# Revit family: Deca_Acabamento para Registro de Gaveta Duna Quadratta_4900.C94.GD
name_source: partatom
category: Plumbing Fixtures
revit_build: Autodesk Revit Architecture 2012 (Build: 20120126_0600(x64)
units: mm (PartAtom-declared; Revit-internal decimal feet)

## types (4) — shared parameters
Aprovado por = Contino/quattroD
Assembly Code = D2020
Atendimento ao Cliente = 0800-0117073
Consumo = Varia com a pressão
Criado por = Contino/quattroD
Description = Acabamento para registro de gaveta
Flow Pressure = 0.00 psi
Linha = Duna Quadratta
Louça/Metais = Metal
Manufacturer = Deca
Material = Deca_Latão Cromado e Plástico de Engenharia
Norma = ABNT NBR 10283: 2003
Peso Liquido (Kg) = 2.96
Pressão = 2 A 40 mca
Produto = Acabamento para registro de gaveta Duna Quadratta
Segmento = Luxo
URL = www.deca.com.br/produtos
Variações de COR = Cromado 1 1/4 e 1 1/2  (4900.C94.GD); Gold 1 1/4 e 1 1/2  (4900.D94.GD.GLD)
zero-valued in all types: CWFU, Default Elevation

## per-type parameters (varying)
| type | Acabamento | Base de Registro de Gaveta_Family | Código | Diâmetro Ponto de Agua | Model | Raio Ponto de Agua |
| 4900.C94.GD_Cromado CR10_1 1/2" | Deca CR10 Cromado Metal | Deca_Shared_Base de Registro de Gaveta_4900.C94.GD : 4509.502 - DN 40 (1 1/2") | 4900.C94.GD | 40 mm  [stored 0.131234 ft] | 4900.C94.GD | 20 mm  [stored 0.0656168 ft] |
| 4900.C94.GD_Cromado CR10_1 1/4" | Deca CR10 Cromado Metal | Deca_Shared_Base de Registro de Gaveta_4900.C94.GD : 4509.402 - DN 32 (1 1/4") | 4900.C94.GD | 32 mm  [stored 0.104987 ft] | 4900.C94.GD | 16 mm  [stored 0.0524934 ft] |
| 4900.D94.GD.GLD_Gold GLD_1 1/4" | Deca GLD Gold Metal | Deca_Shared_Base de Registro de Gaveta_4900.C94.GD : 4509.402 - DN 32 (1 1/4") | 4900.D94.GD.GLD | 32 mm  [stored 0.104987 ft] | 4900.D94.GD.GLD | 16 mm  [stored 0.0524934 ft] |
| 4900.D94.GD.GLD_Gold GLD_1 1/2" | Deca GLD Gold Metal | Deca_Shared_Base de Registro de Gaveta_4900.C94.GD : 4509.502 - DN 40 (1 1/2") | 4900.D94.GD.GLD | 40 mm  [stored 0.131234 ft] | 4900.D94.GD.GLD | 20 mm  [stored 0.0656168 ft] |

note: [stored X ft] marks values corroborated as IEEE doubles in the binary element streams (Revit-internal decimal feet)

## geometry (parser evidence)
native form markers: Blend x4, Sweep x3
no freeform markers — native parametric forms only
